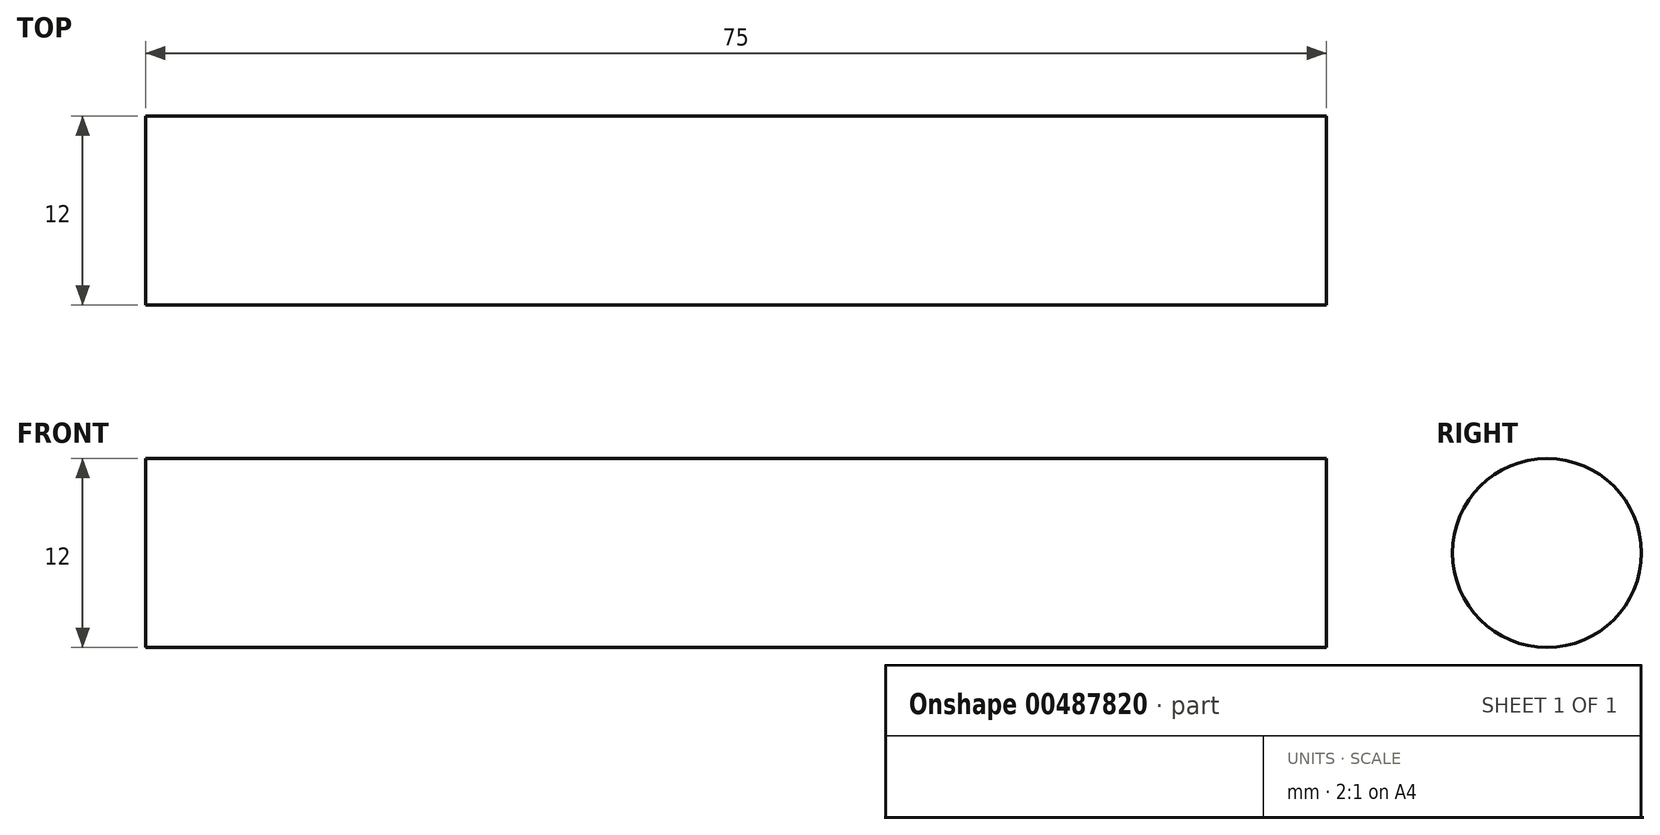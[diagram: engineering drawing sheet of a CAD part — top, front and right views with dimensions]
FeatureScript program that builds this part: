
annotation { "Feature Type Name" : "Feature", "Feature Type Description" : "" }
export const myFeature = defineFeature(function(context is Context, id is Id, definition is map)
    precondition{}
    {
        {
            var Q0;
            Q0=qCreatedBy(makeId("Right.planeOp"),FACE);
            var sketch = newSketch(context, id + "F0", { "sketchPlane" : qUnion([Q0])});
            skCircle(sketch, "E0", {"center": v(0, 0) * mm, "radius": 6 * mm});
            skSolve(sketch);
        }
        {
            var Q0;
            Q0 = qSketchRegion(id + "F0", true);
            extrude(context, id + "F1", {"entities" : qUnion([Q0]), "depth" : 75 * mm, "offsetDistance" : 25 * mm});
        }
    });
